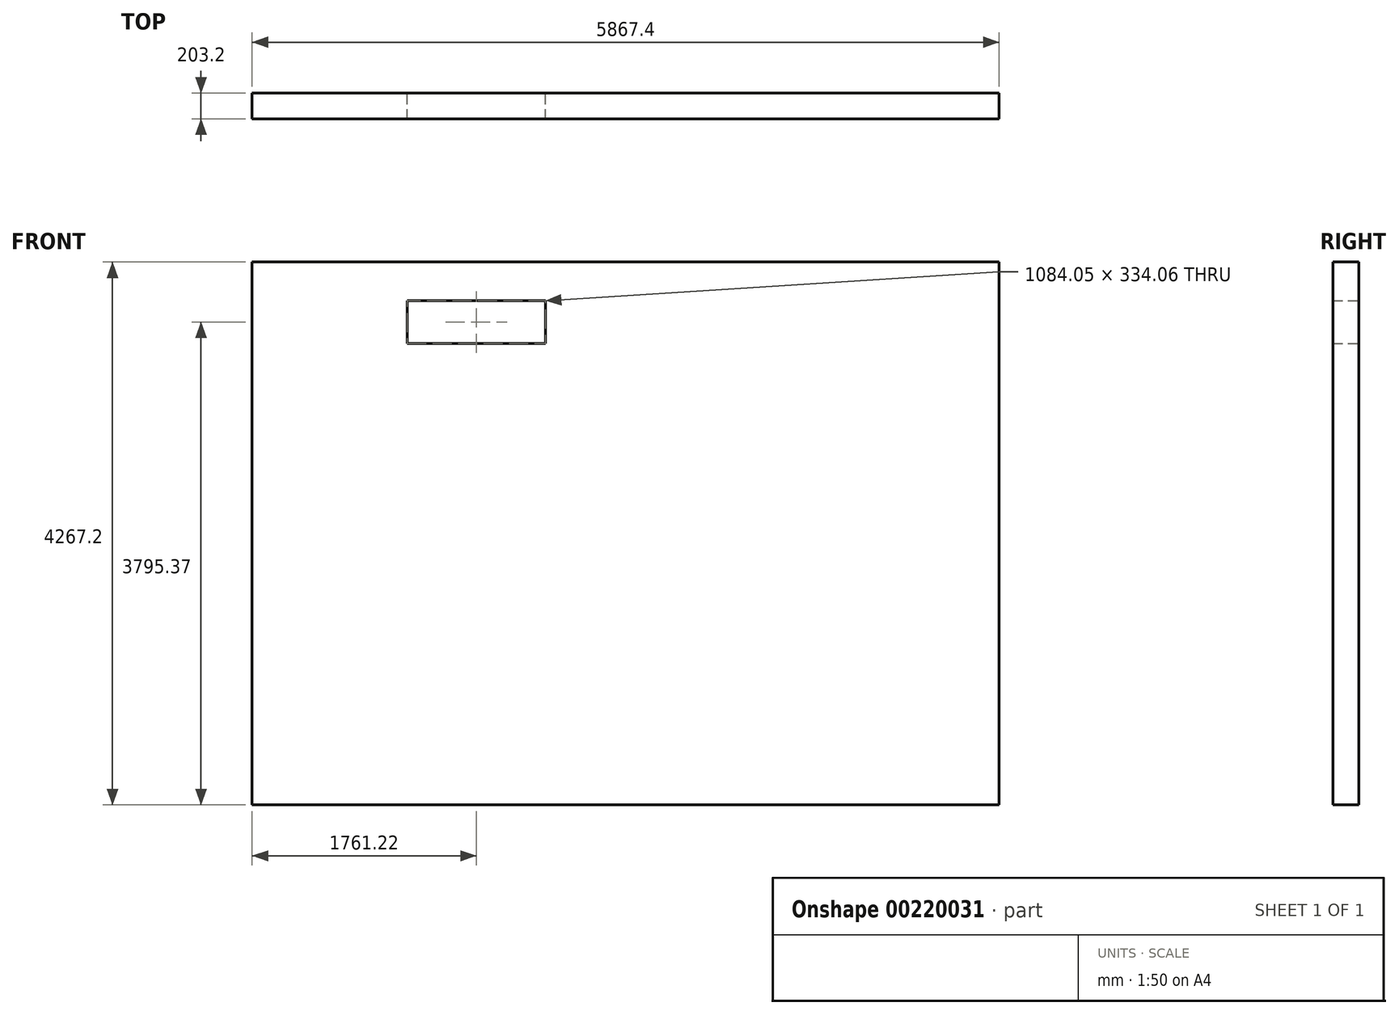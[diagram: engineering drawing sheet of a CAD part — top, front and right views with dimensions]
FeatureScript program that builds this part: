
annotation { "Feature Type Name" : "Feature", "Feature Type Description" : "" }
export const myFeature = defineFeature(function(context is Context, id is Id, definition is map)
    precondition{}
    {
        {
            var Q0;
            Q0=qCreatedBy(makeId("Front.planeOp"),FACE);
            var sketch = newSketch(context, id + "F0", { "sketchPlane" : qUnion([Q0])});
            skLineSegment(sketch, "E0.bottom", {"start": v(0, 0) * mm, "end": v(-5867.4, 0) * mm});
            skLineSegment(sketch, "E0.top", {"start": v(0, 4267.2) * mm, "end": v(-5867.4, 4267.2) * mm});
            skLineSegment(sketch, "E0.left", {"start": v(0, 0) * mm, "end": v(0, 4267.2) * mm});
            skLineSegment(sketch, "E0.right", {"start": v(-5867.4, 0) * mm, "end": v(-5867.4, 4267.2) * mm});
            skLineSegment(sketch, "E1.bottom", {"start": v(-4648.2, 3962.4) * mm, "end": v(-3564.15, 3962.4) * mm});
            skLineSegment(sketch, "E1.top", {"start": v(-4648.2, 3628.34) * mm, "end": v(-3564.15, 3628.34) * mm});
            skLineSegment(sketch, "E1.left", {"start": v(-4648.2, 3962.4) * mm, "end": v(-4648.2, 3628.34) * mm});
            skLineSegment(sketch, "E1.right", {"start": v(-3564.15, 3962.4) * mm, "end": v(-3564.15, 3628.34) * mm});
            skSolve(sketch);
        }
        {
            var Q0;
            Q0=makeQuery(id+"F0.imprint","IMPRINT",FACE,{"disambiguationData":[TD([[makeQuery(id+"F0.imprint","IMPRINT",EDGE,{"derivedFrom":sQuery(id+"F0.wireOp",EDGE,"E0.bottom")}),-1.0]])]});
            extrude(context, id + "F1", {"entities" : qUnion([Q0]), "depth" : 203.2 * mm});
        }
    });
